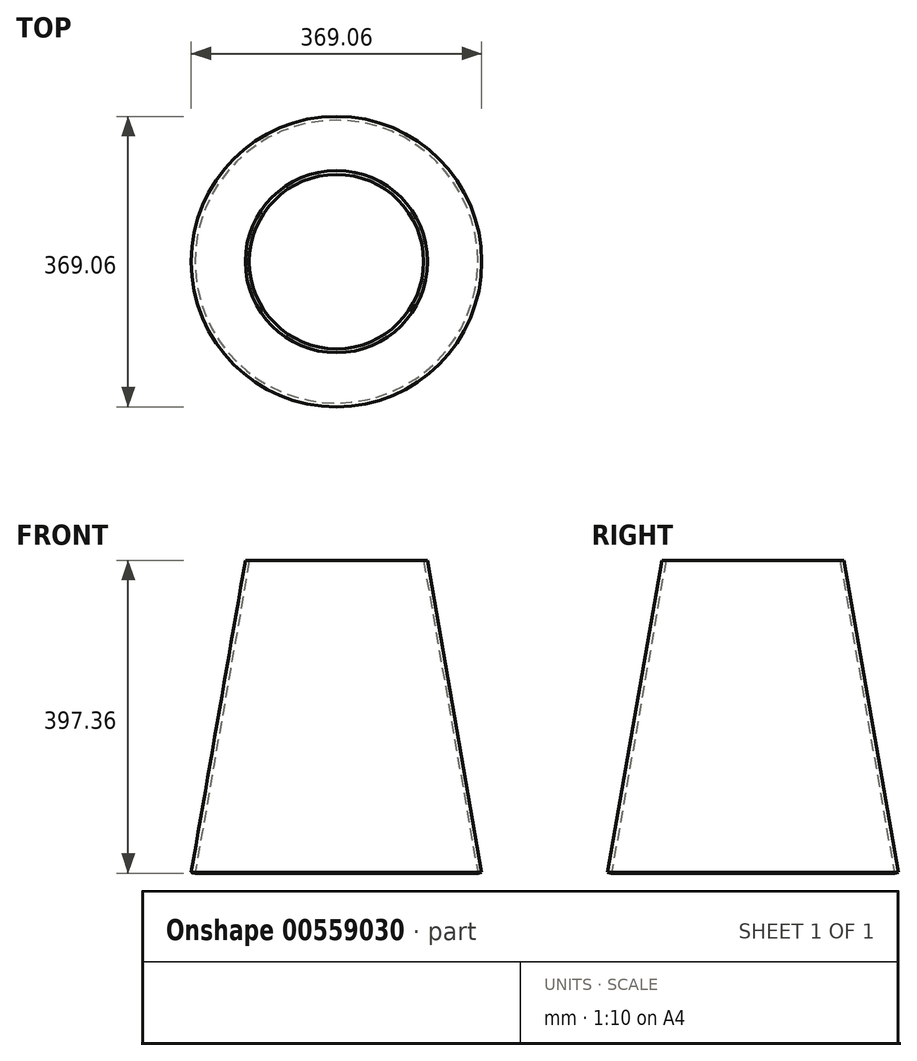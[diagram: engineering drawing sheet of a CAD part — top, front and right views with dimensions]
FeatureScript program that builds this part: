
annotation { "Feature Type Name" : "Feature", "Feature Type Description" : "" }
export const myFeature = defineFeature(function(context is Context, id is Id, definition is map)
    precondition{}
    {
        {
            var Q0;
            Q0=qCreatedBy(makeId("Front.planeOp"),FACE);
            var sketch = newSketch(context, id + "F0", { "sketchPlane" : qUnion([Q0])});
            skLineSegment(sketch, "E0", {"start": v(0, 0) * mm, "end": v(0, 500) * mm, "construction": true});
            skLineSegment(sketch, "E1", {"start": v(179.6, 58) * mm, "end": v(110.75, 454.5) * mm});
            skLineSegment(sketch, "E2", {"start": v(179.6, 58) * mm, "end": v(184.53, 58.86) * mm});
            skLineSegment(sketch, "E3", {"start": v(184.53, 58.86) * mm, "end": v(115.68, 455.36) * mm});
            skLineSegment(sketch, "E4", {"start": v(110.75, 454.5) * mm, "end": v(115.68, 455.36) * mm});
            skSolve(sketch);
        }
        {
            var Q0;
            Q0=makeQuery(id+"F0.imprint","IMPRINT",FACE,{"disambiguationData":[TD([[makeQuery(id+"F0.imprint","IMPRINT",EDGE,{"derivedFrom":sQuery(id+"F0.wireOp",EDGE,"E1")}),-1.0]])]});
            var Q1;
            Q1=sQuery(id+"F0.wireOp",EDGE,"E0");
            revolve(context, id + "F1", {"entities" : qUnion([Q0]), "axis" : qUnion([Q1]), "revolveType" : RevolveType.FULL});
        }
    });
